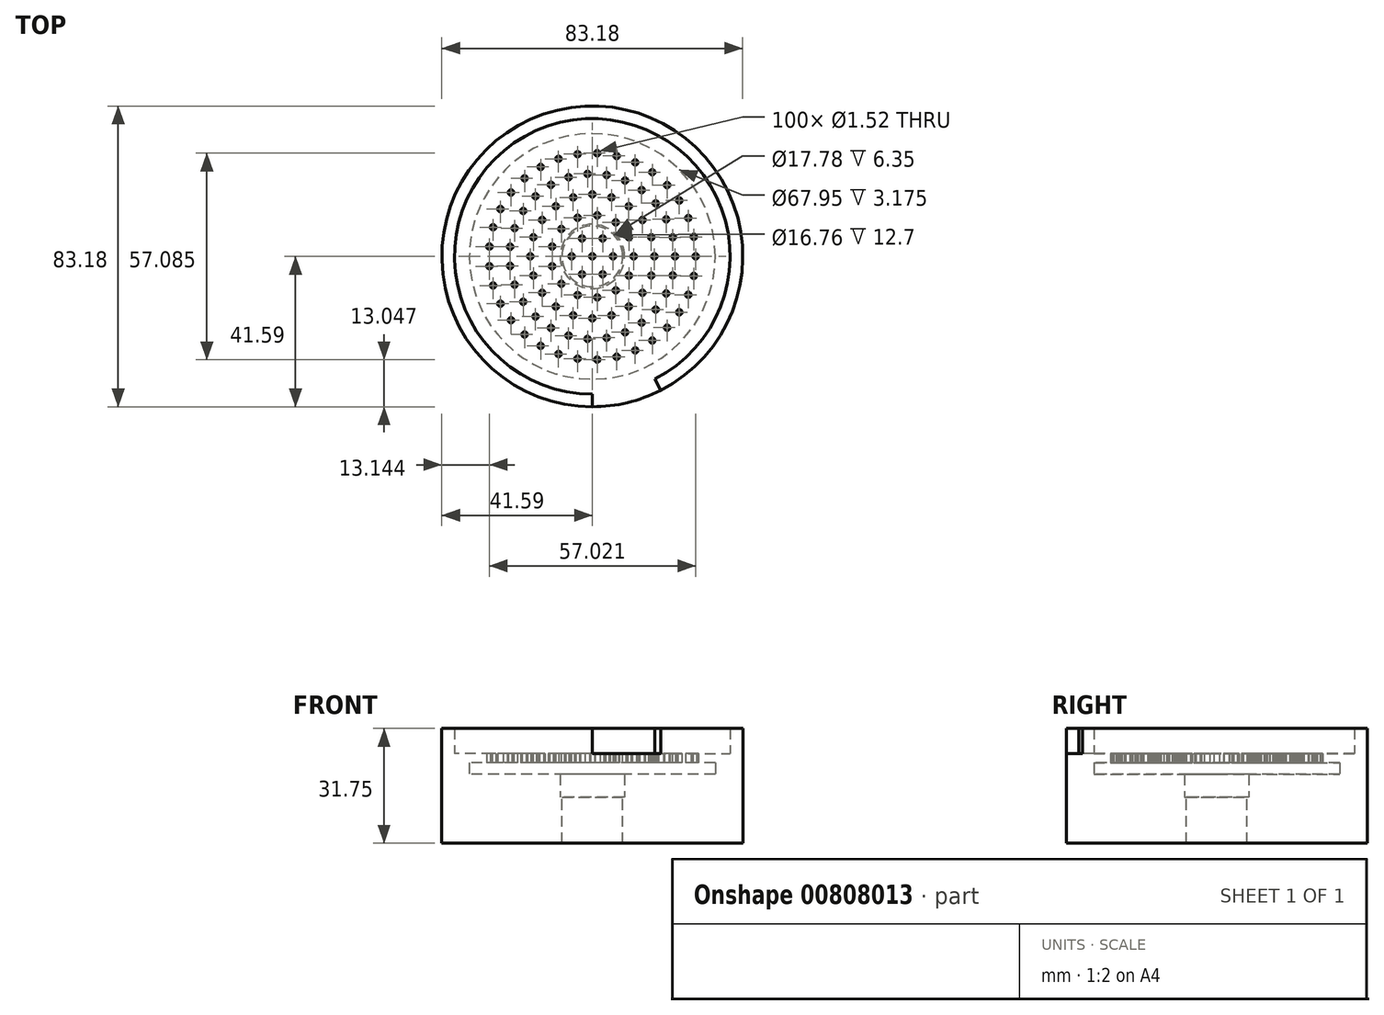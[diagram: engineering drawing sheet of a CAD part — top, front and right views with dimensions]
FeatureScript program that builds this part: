
annotation { "Feature Type Name" : "Feature", "Feature Type Description" : "" }
export const myFeature = defineFeature(function(context is Context, id is Id, definition is map)
    precondition{}
    {
        {
            var Q0;
            Q0=qCreatedBy(makeId("Top.planeOp"),FACE);
            var sketch = newSketch(context, id + "F0", { "sketchPlane" : qUnion([Q0])});
            skCircle(sketch, "E0", {"center": v(0, 0) * mm, "radius": 41.6 * mm});
            skCircle(sketch, "E1", {"center": v(0, 0) * mm, "radius": 8.9 * mm});
            skSolve(sketch);
        }
        {
            var Q0;
            Q0 = qSketchRegion(id + "F0", true);
            extrude(context, id + "F1", {"entities" : qUnion([Q0]), "depth" : 6.35 * mm, "offsetDistance" : 25.4 * mm});
        }
        {
            var Q0;
            Q0=makeQuery(id+"F1.opExtrude","CAP_FACE",FACE,{"disambiguationData":[OSD([sQuery(id+"F0.wireOp",EDGE,"E0"),sQuery(id+"F0.wireOp",EDGE,"E1")])],"isStart":false});
            var sketch = newSketch(context, id + "F2", { "sketchPlane" : qUnion([Q0])});
            skCircle(sketch, "E2", {"center": v(0, 0) * mm, "radius": 41.6 * mm});
            skCircle(sketch, "E3", {"center": v(0, 0) * mm, "radius": 33.97 * mm});
            skSolve(sketch);
        }
        {
            var Q0;
            Q0=makeQuery(id+"F2.imprint","IMPRINT",FACE,{"disambiguationData":[TD([[makeQuery(id+"F2.imprint","IMPRINT",EDGE,{"derivedFrom":sQuery(id+"F2.wireOp",EDGE,"E2")}),1.0]])]});
            extrude(context, id + "F3", {"entities" : qUnion([Q0]), "operationType" : NewBodyOperationType.ADD, "depth" : 3.17 * mm, "offsetDistance" : 25.4 * mm});
        }
        {
            var Q0;
            Q0=makeQuery(id+"F3.opExtrude","CAP_FACE",FACE,{"disambiguationData":[OSD([sQuery(id+"F2.wireOp",EDGE,"E2"),sQuery(id+"F2.wireOp",EDGE,"E3")])],"isStart":false});
            var sketch = newSketch(context, id + "F4", { "sketchPlane" : qUnion([Q0])});
            skCircle(sketch, "E4", {"center": v(0, 0) * mm, "radius": 41.6 * mm});
            skCircle(sketch, "E5", {"center": v(0, 0) * mm, "radius": 0.76 * mm});
            skCircle(sketch, "E6.1.0.0", {"center": v(5.72, 0) * mm, "radius": 0.76 * mm});
            skCircle(sketch, "E6.2.0.0", {"center": v(11.43, 0) * mm, "radius": 0.76 * mm});
            skCircle(sketch, "E6.3.0.0", {"center": v(17.14, 0) * mm, "radius": 0.76 * mm});
            skCircle(sketch, "E6.4.0.0", {"center": v(22.86, 0) * mm, "radius": 0.76 * mm});
            skCircle(sketch, "E6.5.0.0", {"center": v(28.58, 0) * mm, "radius": 0.76 * mm});
            skLineSegment(sketch, "E6.direction1", {"start": v(0, 0) * mm, "end": v(5.72, 0) * mm, "construction": true});
            skCircle(sketch, "E7.1.0", {"center": v(2.86, 4.95) * mm, "radius": 0.76 * mm});
            skCircle(sketch, "E7.2.0", {"center": v(-2.86, 4.95) * mm, "radius": 0.76 * mm});
            skCircle(sketch, "E7.3.0", {"center": v(-5.72, 0) * mm, "radius": 0.76 * mm});
            skCircle(sketch, "E7.4.0", {"center": v(-2.86, -4.95) * mm, "radius": 0.76 * mm});
            skCircle(sketch, "E7.5.0", {"center": v(2.86, -4.95) * mm, "radius": 0.76 * mm});
            skCircle(sketch, "E8.1.0", {"center": v(10.12, 5.31) * mm, "radius": 0.76 * mm});
            skCircle(sketch, "E8.2.0", {"center": v(6.5, 9.4) * mm, "radius": 0.76 * mm});
            skCircle(sketch, "E8.3.0", {"center": v(1.38, 11.35) * mm, "radius": 0.76 * mm});
            skCircle(sketch, "E8.4.0", {"center": v(-4.05, 10.69) * mm, "radius": 0.76 * mm});
            skCircle(sketch, "E8.5.0", {"center": v(-8.56, 7.58) * mm, "radius": 0.76 * mm});
            skCircle(sketch, "E8.6.0", {"center": v(-11.1, 2.74) * mm, "radius": 0.76 * mm});
            skCircle(sketch, "E8.7.0", {"center": v(-11.1, -2.74) * mm, "radius": 0.76 * mm});
            skCircle(sketch, "E8.8.0", {"center": v(-8.56, -7.58) * mm, "radius": 0.76 * mm});
            skCircle(sketch, "E8.9.0", {"center": v(-4.05, -10.69) * mm, "radius": 0.76 * mm});
            skCircle(sketch, "E8.10.0", {"center": v(1.38, -11.35) * mm, "radius": 0.76 * mm});
            skCircle(sketch, "E8.11.0", {"center": v(6.5, -9.4) * mm, "radius": 0.76 * mm});
            skCircle(sketch, "E8.12.0", {"center": v(10.12, -5.31) * mm, "radius": 0.76 * mm});
            skCircle(sketch, "E9.1.0", {"center": v(16.3, 5.3) * mm, "radius": 0.76 * mm});
            skCircle(sketch, "E9.2.0", {"center": v(13.87, 10.08) * mm, "radius": 0.76 * mm});
            skCircle(sketch, "E9.3.0", {"center": v(10.08, 13.87) * mm, "radius": 0.76 * mm});
            skCircle(sketch, "E9.4.0", {"center": v(5.3, 16.3) * mm, "radius": 0.76 * mm});
            skCircle(sketch, "E9.5.0", {"center": v(0, 17.14) * mm, "radius": 0.76 * mm});
            skCircle(sketch, "E9.6.0", {"center": v(-5.3, 16.3) * mm, "radius": 0.76 * mm});
            skCircle(sketch, "E9.7.0", {"center": v(-10.08, 13.87) * mm, "radius": 0.76 * mm});
            skCircle(sketch, "E9.8.0", {"center": v(-13.87, 10.08) * mm, "radius": 0.76 * mm});
            skCircle(sketch, "E9.9.0", {"center": v(-16.3, 5.3) * mm, "radius": 0.76 * mm});
            skCircle(sketch, "E9.10.0", {"center": v(-17.14, 0) * mm, "radius": 0.76 * mm});
            skCircle(sketch, "E9.11.0", {"center": v(-16.3, -5.3) * mm, "radius": 0.76 * mm});
            skCircle(sketch, "E9.12.0", {"center": v(-13.87, -10.08) * mm, "radius": 0.76 * mm});
            skCircle(sketch, "E9.13.0", {"center": v(-10.08, -13.87) * mm, "radius": 0.76 * mm});
            skCircle(sketch, "E9.14.0", {"center": v(-5.3, -16.3) * mm, "radius": 0.76 * mm});
            skCircle(sketch, "E9.15.0", {"center": v(0, -17.14) * mm, "radius": 0.76 * mm});
            skCircle(sketch, "E9.16.0", {"center": v(5.3, -16.3) * mm, "radius": 0.76 * mm});
            skCircle(sketch, "E9.17.0", {"center": v(10.08, -13.87) * mm, "radius": 0.76 * mm});
            skCircle(sketch, "E9.18.0", {"center": v(13.87, -10.08) * mm, "radius": 0.76 * mm});
            skCircle(sketch, "E9.19.0", {"center": v(16.3, -5.3) * mm, "radius": 0.76 * mm});
            skCircle(sketch, "E10.1.0", {"center": v(22.24, 5.27) * mm, "radius": 0.76 * mm});
            skCircle(sketch, "E10.2.0", {"center": v(20.43, 10.26) * mm, "radius": 0.76 * mm});
            skCircle(sketch, "E10.3.0", {"center": v(17.51, 14.7) * mm, "radius": 0.76 * mm});
            skCircle(sketch, "E10.4.0", {"center": v(13.65, 18.34) * mm, "radius": 0.76 * mm});
            skCircle(sketch, "E10.5.0", {"center": v(9.05, 21) * mm, "radius": 0.76 * mm});
            skCircle(sketch, "E10.6.0", {"center": v(3.97, 22.51) * mm, "radius": 0.76 * mm});
            skCircle(sketch, "E10.7.0", {"center": v(-1.33, 22.82) * mm, "radius": 0.76 * mm});
            skCircle(sketch, "E10.8.0", {"center": v(-6.56, 21.9) * mm, "radius": 0.76 * mm});
            skCircle(sketch, "E10.9.0", {"center": v(-11.43, 19.8) * mm, "radius": 0.76 * mm});
            skCircle(sketch, "E10.10.0", {"center": v(-15.69, 16.63) * mm, "radius": 0.76 * mm});
            skCircle(sketch, "E10.11.0", {"center": v(-19.1, 12.56) * mm, "radius": 0.76 * mm});
            skCircle(sketch, "E10.12.0", {"center": v(-21.48, 7.82) * mm, "radius": 0.76 * mm});
            skCircle(sketch, "E10.13.0", {"center": v(-22.7, 2.65) * mm, "radius": 0.76 * mm});
            skCircle(sketch, "E10.14.0", {"center": v(-22.7, -2.65) * mm, "radius": 0.76 * mm});
            skCircle(sketch, "E10.15.0", {"center": v(-21.48, -7.82) * mm, "radius": 0.76 * mm});
            skCircle(sketch, "E10.16.0", {"center": v(-19.1, -12.56) * mm, "radius": 0.76 * mm});
            skCircle(sketch, "E10.17.0", {"center": v(-15.69, -16.63) * mm, "radius": 0.76 * mm});
            skCircle(sketch, "E10.18.0", {"center": v(-11.43, -19.8) * mm, "radius": 0.76 * mm});
            skCircle(sketch, "E10.19.0", {"center": v(-6.56, -21.9) * mm, "radius": 0.76 * mm});
            skCircle(sketch, "E10.20.0", {"center": v(-1.33, -22.82) * mm, "radius": 0.76 * mm});
            skCircle(sketch, "E10.21.0", {"center": v(3.97, -22.51) * mm, "radius": 0.76 * mm});
            skCircle(sketch, "E10.22.0", {"center": v(9.05, -21) * mm, "radius": 0.76 * mm});
            skCircle(sketch, "E10.23.0", {"center": v(13.65, -18.34) * mm, "radius": 0.76 * mm});
            skCircle(sketch, "E10.24.0", {"center": v(17.51, -14.7) * mm, "radius": 0.76 * mm});
            skCircle(sketch, "E10.25.0", {"center": v(20.43, -10.26) * mm, "radius": 0.76 * mm});
            skCircle(sketch, "E10.26.0", {"center": v(22.24, -5.27) * mm, "radius": 0.76 * mm});
            skCircle(sketch, "E11.1.0", {"center": v(28.06, 5.4) * mm, "radius": 0.76 * mm});
            skCircle(sketch, "E11.2.0", {"center": v(26.53, 10.62) * mm, "radius": 0.76 * mm});
            skCircle(sketch, "E11.3.0", {"center": v(24.04, 15.45) * mm, "radius": 0.76 * mm});
            skCircle(sketch, "E11.4.0", {"center": v(20.68, 19.72) * mm, "radius": 0.76 * mm});
            skCircle(sketch, "E11.5.0", {"center": v(16.58, 23.28) * mm, "radius": 0.76 * mm});
            skCircle(sketch, "E11.6.0", {"center": v(11.87, 26) * mm, "radius": 0.76 * mm});
            skCircle(sketch, "E11.7.0", {"center": v(6.74, 27.77) * mm, "radius": 0.76 * mm});
            skCircle(sketch, "E11.8.0", {"center": v(1.36, 28.54) * mm, "radius": 0.76 * mm});
            skCircle(sketch, "E11.9.0", {"center": v(-4.07, 28.28) * mm, "radius": 0.76 * mm});
            skCircle(sketch, "E11.10.0", {"center": v(-9.35, 27) * mm, "radius": 0.76 * mm});
            skCircle(sketch, "E11.11.0", {"center": v(-14.29, 24.75) * mm, "radius": 0.76 * mm});
            skCircle(sketch, "E11.12.0", {"center": v(-18.71, 21.6) * mm, "radius": 0.76 * mm});
            skCircle(sketch, "E11.13.0", {"center": v(-22.46, 17.66) * mm, "radius": 0.76 * mm});
            skCircle(sketch, "E11.14.0", {"center": v(-25.4, 13.1) * mm, "radius": 0.76 * mm});
            skCircle(sketch, "E11.15.0", {"center": v(-27.42, 8.05) * mm, "radius": 0.76 * mm});
            skCircle(sketch, "E11.16.0", {"center": v(-28.45, 2.72) * mm, "radius": 0.76 * mm});
            skCircle(sketch, "E11.17.0", {"center": v(-28.45, -2.72) * mm, "radius": 0.76 * mm});
            skCircle(sketch, "E11.18.0", {"center": v(-27.42, -8.05) * mm, "radius": 0.76 * mm});
            skCircle(sketch, "E11.19.0", {"center": v(-25.4, -13.1) * mm, "radius": 0.76 * mm});
            skCircle(sketch, "E11.20.0", {"center": v(-22.46, -17.66) * mm, "radius": 0.76 * mm});
            skCircle(sketch, "E11.21.0", {"center": v(-18.71, -21.6) * mm, "radius": 0.76 * mm});
            skCircle(sketch, "E11.22.0", {"center": v(-14.29, -24.75) * mm, "radius": 0.76 * mm});
            skCircle(sketch, "E11.23.0", {"center": v(-9.35, -27) * mm, "radius": 0.76 * mm});
            skCircle(sketch, "E11.24.0", {"center": v(-4.07, -28.28) * mm, "radius": 0.76 * mm});
            skCircle(sketch, "E11.25.0", {"center": v(1.36, -28.54) * mm, "radius": 0.76 * mm});
            skCircle(sketch, "E11.26.0", {"center": v(6.74, -27.77) * mm, "radius": 0.76 * mm});
            skCircle(sketch, "E11.27.0", {"center": v(11.87, -26) * mm, "radius": 0.76 * mm});
            skCircle(sketch, "E11.28.0", {"center": v(16.58, -23.28) * mm, "radius": 0.76 * mm});
            skCircle(sketch, "E11.29.0", {"center": v(20.68, -19.72) * mm, "radius": 0.76 * mm});
            skCircle(sketch, "E11.30.0", {"center": v(24.04, -15.45) * mm, "radius": 0.76 * mm});
            skCircle(sketch, "E11.31.0", {"center": v(26.53, -10.62) * mm, "radius": 0.76 * mm});
            skCircle(sketch, "E11.32.0", {"center": v(28.06, -5.4) * mm, "radius": 0.76 * mm});
            skSolve(sketch);
        }
        {
            var Q0;
            Q0=makeQuery(id+"F4.imprint","IMPRINT",FACE,{"disambiguationData":[TD([[makeQuery(id+"F4.imprint","IMPRINT",EDGE,{"derivedFrom":sQuery(id+"F4.wireOp",EDGE,"E4")}),1.0]])]});
            var Q1;
            Q1=makeQuery(id+"F4.imprint","IMPRINT",FACE,{"disambiguationData":[TD([[makeQuery(id+"F4.imprint","IMPRINT",EDGE,{"derivedFrom":sQuery(id+"F4.wireOp",EDGE,"E5")}),-1.0]])]});
            extrude(context, id + "F5", {"entities" : qUnion([Q0, Q1]), "operationType" : NewBodyOperationType.ADD, "depth" : 2.54 * mm, "offsetDistance" : 25.4 * mm});
        }
        {
            var Q0;
            Q0=makeQuery(id+"F5.opExtrude","CAP_FACE",FACE,{"disambiguationData":[OSD([sQuery(id+"F4.wireOp",EDGE,"E4"),sQuery(id+"F4.wireOp",EDGE,"E5"),sQuery(id+"F4.wireOp",EDGE,"E6.1.0.0"),sQuery(id+"F4.wireOp",EDGE,"E6.2.0.0"),sQuery(id+"F4.wireOp",EDGE,"E6.3.0.0"),sQuery(id+"F4.wireOp",EDGE,"E6.4.0.0"),sQuery(id+"F4.wireOp",EDGE,"E6.5.0.0"),sQuery(id+"F4.wireOp",EDGE,"E7.1.0"),sQuery(id+"F4.wireOp",EDGE,"E7.2.0"),sQuery(id+"F4.wireOp",EDGE,"E7.3.0"),sQuery(id+"F4.wireOp",EDGE,"E7.4.0"),sQuery(id+"F4.wireOp",EDGE,"E7.5.0"),sQuery(id+"F4.wireOp",EDGE,"E8.1.0"),sQuery(id+"F4.wireOp",EDGE,"E8.2.0"),sQuery(id+"F4.wireOp",EDGE,"E8.3.0"),sQuery(id+"F4.wireOp",EDGE,"E8.4.0"),sQuery(id+"F4.wireOp",EDGE,"E8.5.0"),sQuery(id+"F4.wireOp",EDGE,"E8.6.0"),sQuery(id+"F4.wireOp",EDGE,"E8.7.0"),sQuery(id+"F4.wireOp",EDGE,"E8.8.0"),sQuery(id+"F4.wireOp",EDGE,"E8.9.0"),sQuery(id+"F4.wireOp",EDGE,"E8.10.0"),sQuery(id+"F4.wireOp",EDGE,"E8.11.0"),sQuery(id+"F4.wireOp",EDGE,"E8.12.0"),sQuery(id+"F4.wireOp",EDGE,"E9.1.0"),sQuery(id+"F4.wireOp",EDGE,"E9.2.0"),sQuery(id+"F4.wireOp",EDGE,"E9.3.0"),sQuery(id+"F4.wireOp",EDGE,"E9.4.0"),sQuery(id+"F4.wireOp",EDGE,"E9.5.0"),sQuery(id+"F4.wireOp",EDGE,"E9.6.0"),sQuery(id+"F4.wireOp",EDGE,"E9.7.0"),sQuery(id+"F4.wireOp",EDGE,"E9.8.0"),sQuery(id+"F4.wireOp",EDGE,"E9.9.0"),sQuery(id+"F4.wireOp",EDGE,"E9.10.0"),sQuery(id+"F4.wireOp",EDGE,"E9.11.0"),sQuery(id+"F4.wireOp",EDGE,"E9.12.0"),sQuery(id+"F4.wireOp",EDGE,"E9.13.0"),sQuery(id+"F4.wireOp",EDGE,"E9.14.0"),sQuery(id+"F4.wireOp",EDGE,"E9.15.0"),sQuery(id+"F4.wireOp",EDGE,"E9.16.0"),sQuery(id+"F4.wireOp",EDGE,"E9.17.0"),sQuery(id+"F4.wireOp",EDGE,"E9.18.0"),sQuery(id+"F4.wireOp",EDGE,"E9.19.0"),sQuery(id+"F4.wireOp",EDGE,"E10.1.0"),sQuery(id+"F4.wireOp",EDGE,"E10.2.0"),sQuery(id+"F4.wireOp",EDGE,"E10.3.0"),sQuery(id+"F4.wireOp",EDGE,"E10.4.0"),sQuery(id+"F4.wireOp",EDGE,"E10.5.0"),sQuery(id+"F4.wireOp",EDGE,"E10.6.0"),sQuery(id+"F4.wireOp",EDGE,"E10.7.0"),sQuery(id+"F4.wireOp",EDGE,"E10.8.0"),sQuery(id+"F4.wireOp",EDGE,"E10.9.0"),sQuery(id+"F4.wireOp",EDGE,"E10.10.0"),sQuery(id+"F4.wireOp",EDGE,"E10.11.0"),sQuery(id+"F4.wireOp",EDGE,"E10.12.0"),sQuery(id+"F4.wireOp",EDGE,"E10.13.0"),sQuery(id+"F4.wireOp",EDGE,"E10.14.0"),sQuery(id+"F4.wireOp",EDGE,"E10.15.0"),sQuery(id+"F4.wireOp",EDGE,"E10.16.0"),sQuery(id+"F4.wireOp",EDGE,"E10.17.0"),sQuery(id+"F4.wireOp",EDGE,"E10.18.0"),sQuery(id+"F4.wireOp",EDGE,"E10.19.0"),sQuery(id+"F4.wireOp",EDGE,"E10.20.0"),sQuery(id+"F4.wireOp",EDGE,"E10.21.0"),sQuery(id+"F4.wireOp",EDGE,"E10.22.0"),sQuery(id+"F4.wireOp",EDGE,"E10.23.0"),sQuery(id+"F4.wireOp",EDGE,"E10.24.0"),sQuery(id+"F4.wireOp",EDGE,"E10.25.0"),sQuery(id+"F4.wireOp",EDGE,"E10.26.0"),sQuery(id+"F4.wireOp",EDGE,"E11.1.0"),sQuery(id+"F4.wireOp",EDGE,"E11.2.0"),sQuery(id+"F4.wireOp",EDGE,"E11.3.0"),sQuery(id+"F4.wireOp",EDGE,"E11.4.0"),sQuery(id+"F4.wireOp",EDGE,"E11.5.0"),sQuery(id+"F4.wireOp",EDGE,"E11.6.0"),sQuery(id+"F4.wireOp",EDGE,"E11.7.0"),sQuery(id+"F4.wireOp",EDGE,"E11.8.0"),sQuery(id+"F4.wireOp",EDGE,"E11.9.0"),sQuery(id+"F4.wireOp",EDGE,"E11.10.0"),sQuery(id+"F4.wireOp",EDGE,"E11.11.0"),sQuery(id+"F4.wireOp",EDGE,"E11.12.0"),sQuery(id+"F4.wireOp",EDGE,"E11.13.0"),sQuery(id+"F4.wireOp",EDGE,"E11.14.0"),sQuery(id+"F4.wireOp",EDGE,"E11.15.0"),sQuery(id+"F4.wireOp",EDGE,"E11.16.0"),sQuery(id+"F4.wireOp",EDGE,"E11.17.0"),sQuery(id+"F4.wireOp",EDGE,"E11.18.0"),sQuery(id+"F4.wireOp",EDGE,"E11.19.0"),sQuery(id+"F4.wireOp",EDGE,"E11.20.0"),sQuery(id+"F4.wireOp",EDGE,"E11.21.0"),sQuery(id+"F4.wireOp",EDGE,"E11.22.0"),sQuery(id+"F4.wireOp",EDGE,"E11.23.0"),sQuery(id+"F4.wireOp",EDGE,"E11.24.0"),sQuery(id+"F4.wireOp",EDGE,"E11.25.0"),sQuery(id+"F4.wireOp",EDGE,"E11.26.0"),sQuery(id+"F4.wireOp",EDGE,"E11.27.0"),sQuery(id+"F4.wireOp",EDGE,"E11.28.0"),sQuery(id+"F4.wireOp",EDGE,"E11.29.0"),sQuery(id+"F4.wireOp",EDGE,"E11.30.0"),sQuery(id+"F4.wireOp",EDGE,"E11.31.0"),sQuery(id+"F4.wireOp",EDGE,"E11.32.0")])],"isStart":false});
            var sketch = newSketch(context, id + "F6", { "sketchPlane" : qUnion([Q0])});
            skCircle(sketch, "E12", {"center": v(0, 0) * mm, "radius": 41.6 * mm});
            skCircle(sketch, "E13", {"center": v(0, 0) * mm, "radius": 38.1 * mm});
            skLineSegment(sketch, "E14", {"start": v(0, 0) * mm, "end": v(0, -41.6) * mm});
            skLineSegment(sketch, "E15", {"start": v(0, -38.1) * mm, "end": v(17.29, -33.95) * mm});
            skLineSegment(sketch, "E16", {"start": v(17.29, -33.95) * mm, "end": v(0, 0) * mm});
            skLineSegment(sketch, "E17", {"start": v(0, 0) * mm, "end": v(18.87, -37.06) * mm});
            skSolve(sketch);
        }
        {
            var Q0;
            {var subQ0=sQuery(id+"F6.wireOp",EDGE,"E14");var subQ1=sQuery(id+"F6.wireOp",EDGE,"E12");var subQ2=makeQuery(id+"F6.imprint","INTERSECT",VERTEX,{"derivedFrom":[subQ1,subQ0]});Q0=makeQuery(id+"F6.imprint","IMPRINT",FACE,{"disambiguationData":[TD([[makeQuery(id+"F6.imprint","IMPRINT",EDGE,{"disambiguationData":[TD([[subQ2,1.0]])],"derivedFrom":subQ1}),1.0]])]});}
            extrude(context, id + "F7", {"entities" : qUnion([Q0]), "operationType" : NewBodyOperationType.ADD, "depth" : 7 * mm, "offsetDistance" : 25.4 * mm});
        }
        {
            var Q0;
            Q0=makeQuery(id+"F1.opExtrude","CAP_FACE",FACE,{"disambiguationData":[OSD([sQuery(id+"F0.wireOp",EDGE,"E0"),sQuery(id+"F0.wireOp",EDGE,"E1")])],"isStart":true});
            var sketch = newSketch(context, id + "F8", { "sketchPlane" : qUnion([Q0])});
            skLineSegment(sketch, "E18.bottom", {"start": v(-25.4, 25.4) * mm, "end": v(25.4, 25.4) * mm});
            skLineSegment(sketch, "E18.top", {"start": v(-25.4, -25.4) * mm, "end": v(25.4, -25.4) * mm});
            skLineSegment(sketch, "E18.left", {"start": v(-25.4, 25.4) * mm, "end": v(-25.4, -25.4) * mm});
            skLineSegment(sketch, "E18.right", {"start": v(25.4, 25.4) * mm, "end": v(25.4, -25.4) * mm});
            skPoint(sketch, "E18.middle", {"position": v(0, 0) * mm});
            skCircle(sketch, "E19", {"center": v(0, 0) * mm, "radius": 8.38 * mm});
            skSolve(sketch);
        }
        {
            var Q0;
            Q0=makeQuery(id+"F8.imprint","IMPRINT",FACE,{"disambiguationData":[TD([[makeQuery(id+"F8.imprint","IMPRINT",EDGE,{"derivedFrom":sQuery(id+"F8.wireOp",EDGE,"E18.bottom")}),-1.0]])]});
            var Q1;
            Q1=makeQuery(id+"F8.imprint","IMPRINT",FACE,{"disambiguationData":[TD([[makeQuery(id+"F8.imprint","IMPRINT",EDGE,{"derivedFrom":sQuery(id+"F8.wireOp",EDGE,"E18.bottom")}),1.0]])]});
            var Q2;
            Q2=makeQuery(id+"F8.imprint","IMPRINT",FACE,{"disambiguationData":[TD([[makeQuery(id+"F8.imprint","IMPRINT",EDGE,{"derivedFrom":sQuery(id+"F8.wireOp",EDGE,"E19")}),-1.0]])]});
            extrude(context, id + "F9", {"entities" : qUnion([Q0, Q1, Q2]), "operationType" : NewBodyOperationType.ADD, "depth" : 12.7 * mm, "offsetDistance" : 25.4 * mm});
        }
    });
